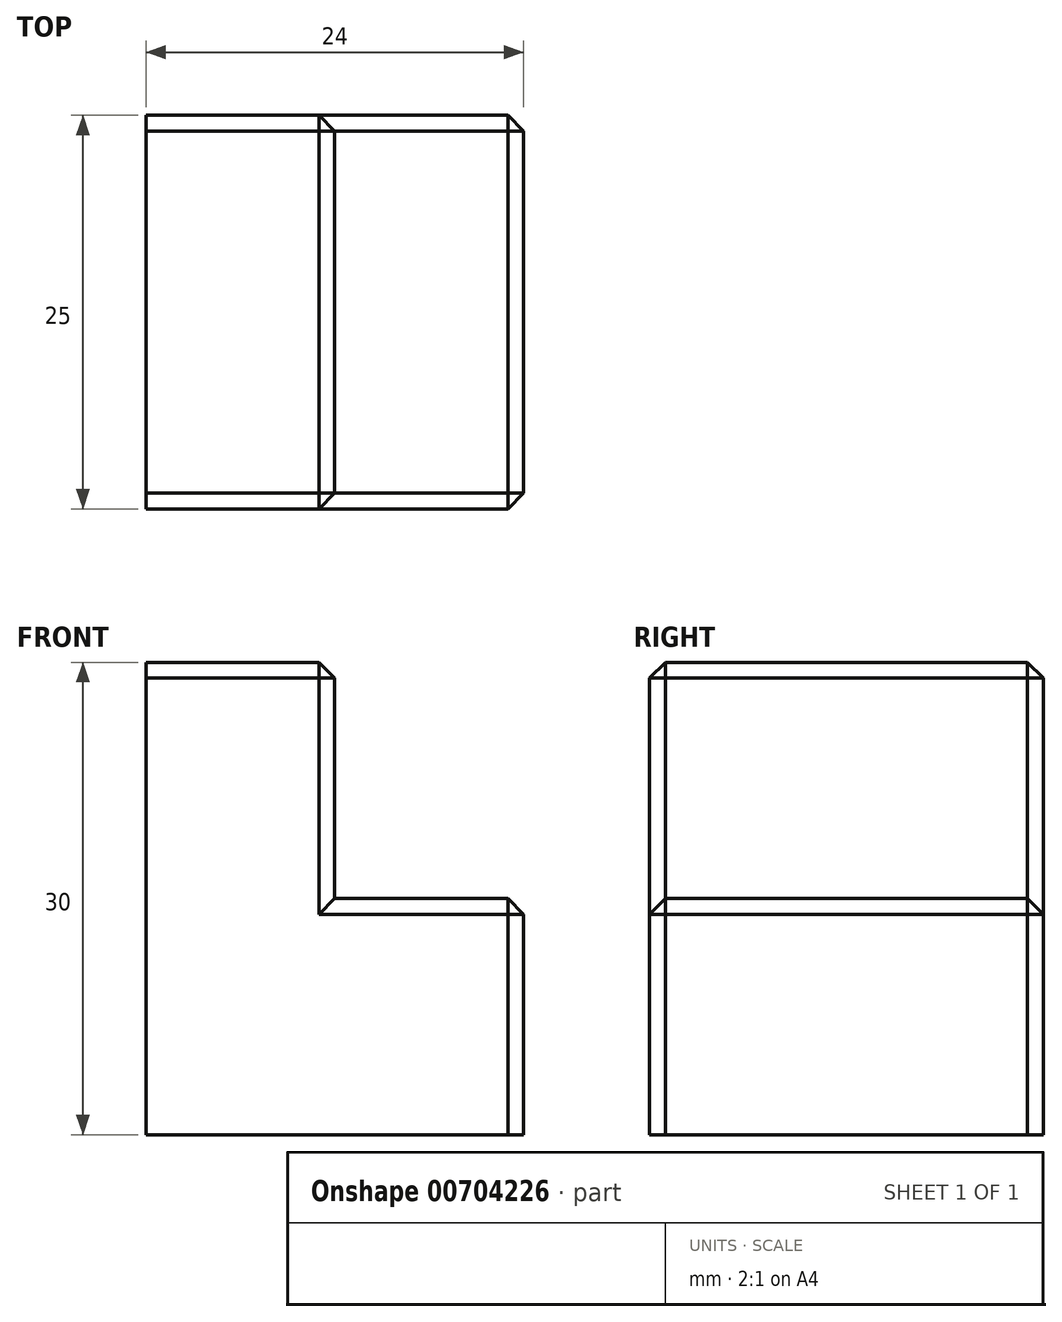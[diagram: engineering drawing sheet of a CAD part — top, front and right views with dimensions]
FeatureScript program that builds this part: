
annotation { "Feature Type Name" : "Feature", "Feature Type Description" : "" }
export const myFeature = defineFeature(function(context is Context, id is Id, definition is map)
    precondition{}
    {
        {
            var Q0;
            Q0=qCreatedBy(makeId("Front.planeOp"),FACE);
            var sketch = newSketch(context, id + "F0", { "sketchPlane" : qUnion([Q0])});
            skLineSegment(sketch, "E0", {"start": v(0, 0) * mm, "end": v(0, 15) * mm});
            skLineSegment(sketch, "E1", {"start": v(0, 15) * mm, "end": v(-12, 15) * mm});
            skLineSegment(sketch, "E2", {"start": v(-12, 15) * mm, "end": v(-12, -15) * mm});
            skLineSegment(sketch, "E3", {"start": v(-12, -15) * mm, "end": v(12, -15) * mm});
            skLineSegment(sketch, "E4", {"start": v(12, -15) * mm, "end": v(12, 0) * mm});
            skLineSegment(sketch, "E5", {"start": v(12, 0) * mm, "end": v(0, 0) * mm});
            skSolve(sketch);
        }
        {
            var Q0;
            Q0 = qSketchRegion(id + "F0", true);
            extrude(context, id + "F1", {"entities" : qUnion([Q0]), "oppositeDirection" : true, "depth" : 25 * mm, "offsetDistance" : 25 * mm});
        }
        {
            var Q0;
            Q0=makeQuery(id+"F1.opExtrude","CAP_EDGE",EDGE,{"disambiguationData":[OSD([sQuery(id+"F0.wireOp",EDGE,"E0")])],"isStart":true});
            var Q1;
            Q1=makeQuery(id+"F1.opExtrude","SWEPT_EDGE",EDGE,{"disambiguationData":[OSD([sQuery(id+"F0.wireOp",EDGE,"E0"),sQuery(id+"F0.wireOp",EDGE,"E1")])]});
            var Q2;
            Q2=makeQuery(id+"F1.opExtrude","CAP_EDGE",EDGE,{"disambiguationData":[OSD([sQuery(id+"F0.wireOp",EDGE,"E5")])],"isStart":true});
            var Q3;
            Q3=makeQuery(id+"F1.opExtrude","SWEPT_EDGE",EDGE,{"disambiguationData":[OSD([sQuery(id+"F0.wireOp",EDGE,"E4"),sQuery(id+"F0.wireOp",EDGE,"E5")])]});
            var Q4;
            Q4=makeQuery(id+"F1.opExtrude","CAP_EDGE",EDGE,{"disambiguationData":[OSD([sQuery(id+"F0.wireOp",EDGE,"E4")])],"isStart":true});
            var Q5;
            Q5=makeQuery(id+"F1.opExtrude","CAP_EDGE",EDGE,{"disambiguationData":[OSD([sQuery(id+"F0.wireOp",EDGE,"E0")])],"isStart":false});
            var Q6;
            Q6=makeQuery(id+"F1.opExtrude","CAP_EDGE",EDGE,{"disambiguationData":[OSD([sQuery(id+"F0.wireOp",EDGE,"E5")])],"isStart":false});
            var Q7;
            Q7=makeQuery(id+"F1.opExtrude","CAP_EDGE",EDGE,{"disambiguationData":[OSD([sQuery(id+"F0.wireOp",EDGE,"E4")])],"isStart":false});
            var Q8;
            Q8=makeQuery(id+"F1.opExtrude","CAP_EDGE",EDGE,{"disambiguationData":[OSD([sQuery(id+"F0.wireOp",EDGE,"E1")])],"isStart":false});
            var Q9;
            Q9=makeQuery(id+"F1.opExtrude","CAP_EDGE",EDGE,{"disambiguationData":[OSD([sQuery(id+"F0.wireOp",EDGE,"E1")])],"isStart":true});
            chamfer(context, id + "F2", {"entities" : qUnion([Q0, Q1, Q2, Q3, Q4, Q5, Q6, Q7, Q8, Q9]), "width" : 1 * mm, "tangentPropagation" : true});
        }
    });
